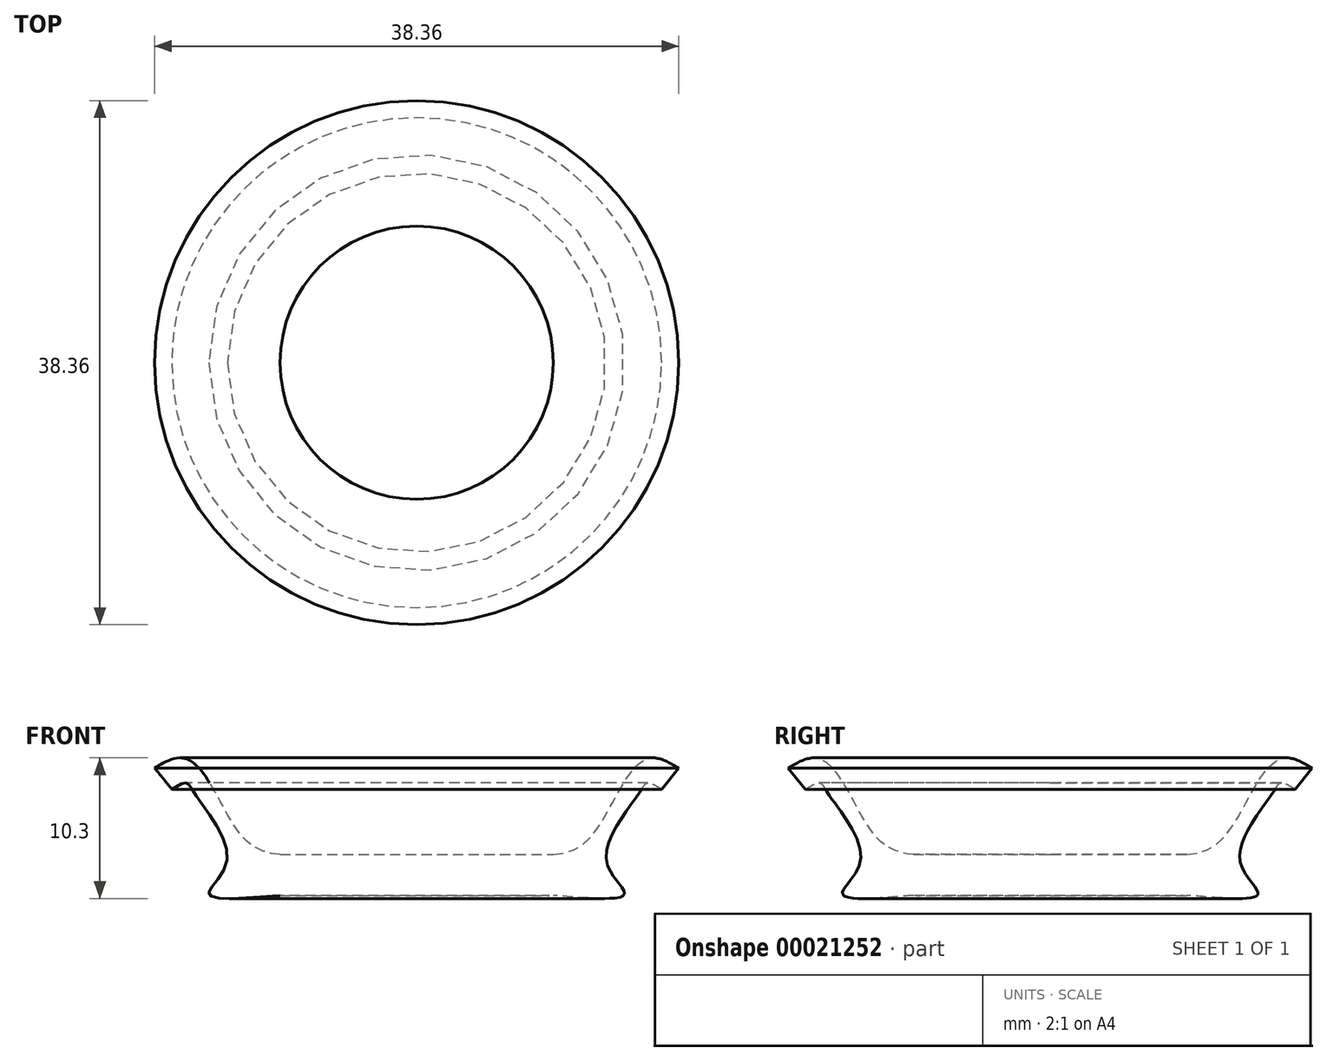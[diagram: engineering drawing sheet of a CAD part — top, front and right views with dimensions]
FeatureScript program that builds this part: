
annotation { "Feature Type Name" : "Feature", "Feature Type Description" : "" }
export const myFeature = defineFeature(function(context is Context, id is Id, definition is map)
    precondition{}
    {
        {
            var Q0;
            Q0=qCreatedBy(makeId("Front.planeOp"),FACE);
            var sketch = newSketch(context, id + "F0", { "sketchPlane" : qUnion([Q0])});
            skLineSegment(sketch, "E0.bottom", {"start": v(0, 0) * mm, "end": v(10, 0) * mm});
            skLineSegment(sketch, "E0.top", {"start": v(0, 3) * mm, "end": v(10, 3) * mm});
            skLineSegment(sketch, "E0.left", {"start": v(0, 0) * mm, "end": v(0, 3) * mm});
            skLineSegment(sketch, "E0.right", {"start": v(10, 0) * mm, "end": v(10, 3) * mm});
            skFitSpline(sketch, "E1", {"points": [v(10, 0) * mm, v(15.15, 0) * mm, v(13.9, 2.44) * mm, v(16.26, 7.47) * mm, v(16.93, 8.24) * mm, v(17.92, 7.78) * mm], "startDerivative": vector(7.73, 0) * mm, "endDerivative": vector(6.75, -3.45) * mm});
            skFitSpline(sketch, "E2", {"points": [v(10, 3) * mm, v(12.62, 4.16) * mm, v(14.87, 7.79) * mm, v(17.13, 10.07) * mm, v(19.18, 9.34) * mm], "startDerivative": vector(13.13, 0.84) * mm, "endDerivative": vector(7.25, -3.96) * mm});
            skLineSegment(sketch, "E3", {"start": v(19.18, 9.34) * mm, "end": v(17.92, 7.78) * mm});
            skSolve(sketch);
        }
        {
            var Q0;
            Q0=makeQuery(id+"F0.imprint","IMPRINT",FACE,{"disambiguationData":[TD([[makeQuery(id+"F0.imprint","IMPRINT",EDGE,{"derivedFrom":sQuery(id+"F0.wireOp",EDGE,"E0.bottom")}),1.0]])]});
            var Q1;
            Q1=makeQuery(id+"F0.imprint","IMPRINT",FACE,{"disambiguationData":[TD([[makeQuery(id+"F0.imprint","IMPRINT",EDGE,{"derivedFrom":sQuery(id+"F0.wireOp",EDGE,"E0.right")}),-1.0]])]});
            var Q2;
            Q2=sQuery(id+"F0.wireOp",EDGE,"E0.left");
            revolve(context, id + "F1", {"entities" : qUnion([Q0, Q1]), "axis" : qUnion([Q2]), "revolveType" : RevolveType.FULL});
        }
    });
